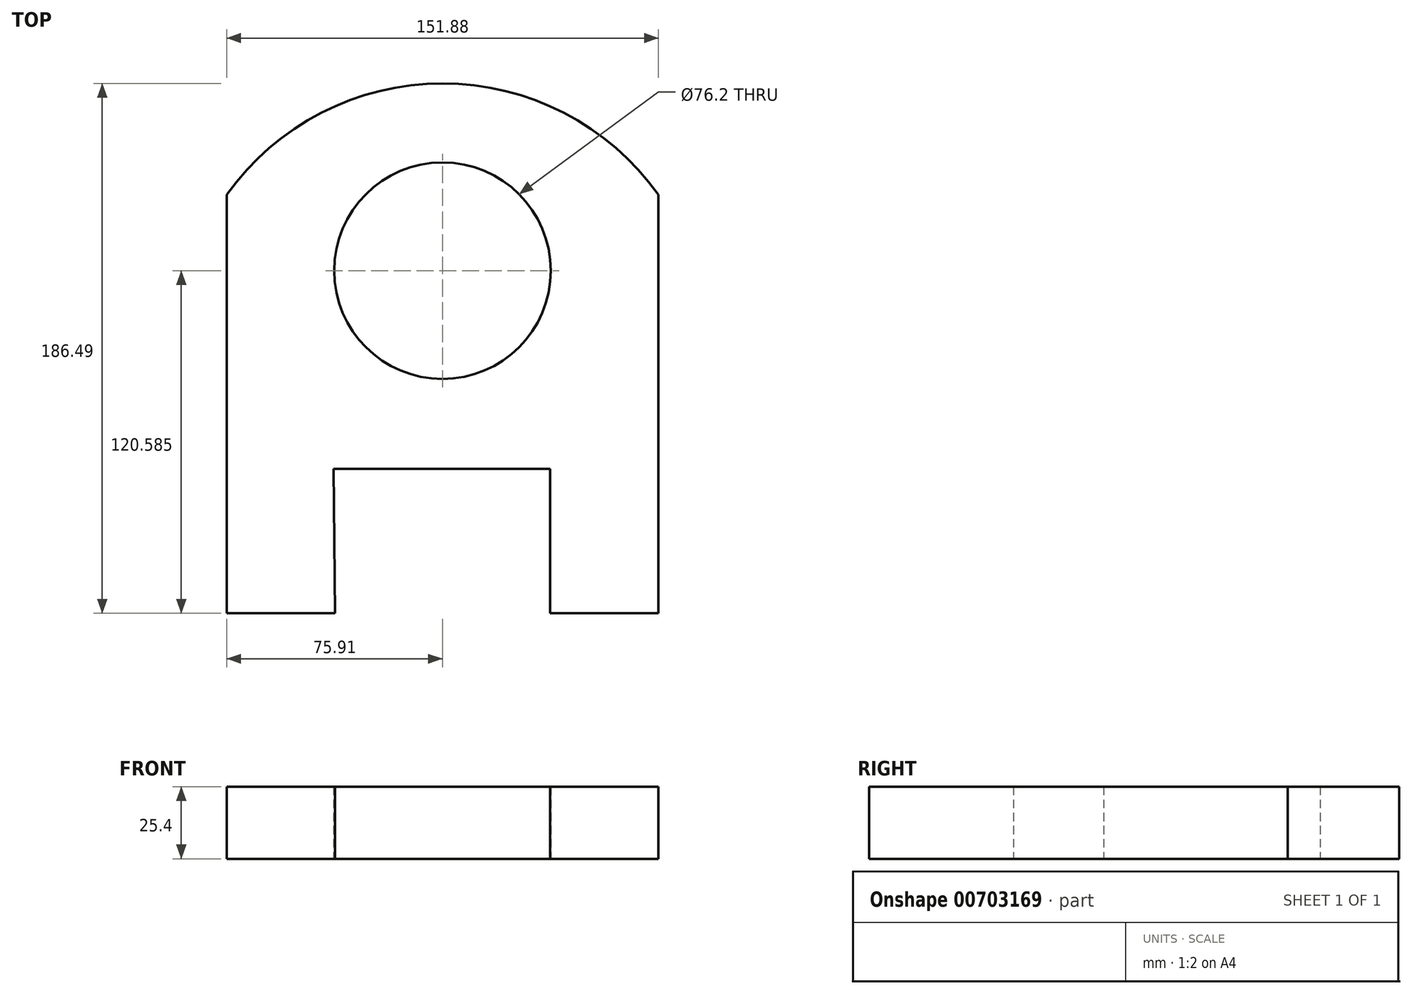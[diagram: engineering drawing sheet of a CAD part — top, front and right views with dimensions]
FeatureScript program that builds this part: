
annotation { "Feature Type Name" : "Feature", "Feature Type Description" : "" }
export const myFeature = defineFeature(function(context is Context, id is Id, definition is map)
    precondition{}
    {
        {
            var Q0;
            Q0=qCreatedBy(makeId("Top.planeOp"),FACE);
            var sketch = newSketch(context, id + "F0", { "sketchPlane" : qUnion([Q0])});
            skLineSegment(sketch, "E0", {"start": v(-38.33, 0) * mm, "end": v(37.87, 0) * mm});
            skLineSegment(sketch, "E1", {"start": v(-75.9, -50.8) * mm, "end": v(-37.8, -50.8) * mm});
            skLineSegment(sketch, "E2", {"start": v(37.87, -50.8) * mm, "end": v(75.97, -50.8) * mm});
            skLineSegment(sketch, "E3", {"start": v(-38.33, 0) * mm, "end": v(-37.8, -50.8) * mm});
            skLineSegment(sketch, "E4", {"start": v(37.87, 0) * mm, "end": v(37.87, -50.8) * mm});
            skArc(sketch, "E5", {"start": v(75.97, 96.52) * mm, "mid": v(0.03, 135.7) * mm, "end": v(-75.9, 96.52) * mm});
            skLineSegment(sketch, "E6", {"start": v(-75.9, 0) * mm, "end": v(-75.9, -50.8) * mm});
            skLineSegment(sketch, "E7", {"start": v(-75.9, 0) * mm, "end": v(-75.9, 96.52) * mm});
            skLineSegment(sketch, "E8", {"start": v(75.97, 0) * mm, "end": v(75.97, -50.8) * mm});
            skLineSegment(sketch, "E9", {"start": v(75.97, 96.52) * mm, "end": v(75.97, 0) * mm});
            skSolve(sketch);
        }
        {
            var Q0;
            Q0=makeQuery(id+"F0.imprint","IMPRINT",FACE,{"disambiguationData":[TD([[makeQuery(id+"F0.imprint","IMPRINT",EDGE,{"derivedFrom":sQuery(id+"F0.wireOp",EDGE,"E0")}),1.0]])]});
            extrude(context, id + "F1", {"entities" : qUnion([Q0]), "depth" : 25.4 * mm, "offsetDistance" : 25.4 * mm});
        }
        {
            var Q0;
            Q0=qCreatedBy(makeId("Top.planeOp"),FACE);
            var sketch = newSketch(context, id + "F2", { "sketchPlane" : qUnion([Q0])});
            skPoint(sketch, "E10", {"position": v(0, 69.79) * mm});
            skSolve(sketch);
        }
        {
            var Q0;
            Q0=sQuery(id+"F2.wireOp",VERTEX,"E10");
            var Q1;
            Q1=makeQuery(id+"F1.opExtrude","SWEPT_BODY",BODY,{"disambiguationData":[OSD([sQuery(id+"F0.wireOp",EDGE,"E0"),sQuery(id+"F0.wireOp",EDGE,"E1"),sQuery(id+"F0.wireOp",EDGE,"E2"),sQuery(id+"F0.wireOp",EDGE,"E3"),sQuery(id+"F0.wireOp",EDGE,"E4"),sQuery(id+"F0.wireOp",EDGE,"E5"),sQuery(id+"F0.wireOp",EDGE,"E6"),sQuery(id+"F0.wireOp",EDGE,"E7"),sQuery(id+"F0.wireOp",EDGE,"E8"),sQuery(id+"F0.wireOp",EDGE,"E9")])]});
            hole(context, id + "F3", {"style" : HoleStyle.SIMPLE, "endStyle" : HoleEndStyle.THROUGH, "oppositeDirection" : true, "holeDiameter" : 76.2 * mm, "majorDiameter" : 6.35 * mm, "isTappedThrough" : true, "tappedDepth" : 12.7 * mm, "tapClearance" : 3, "locations" : qUnion([Q0]), "scope" : qUnion([Q1])});
        }
    });
